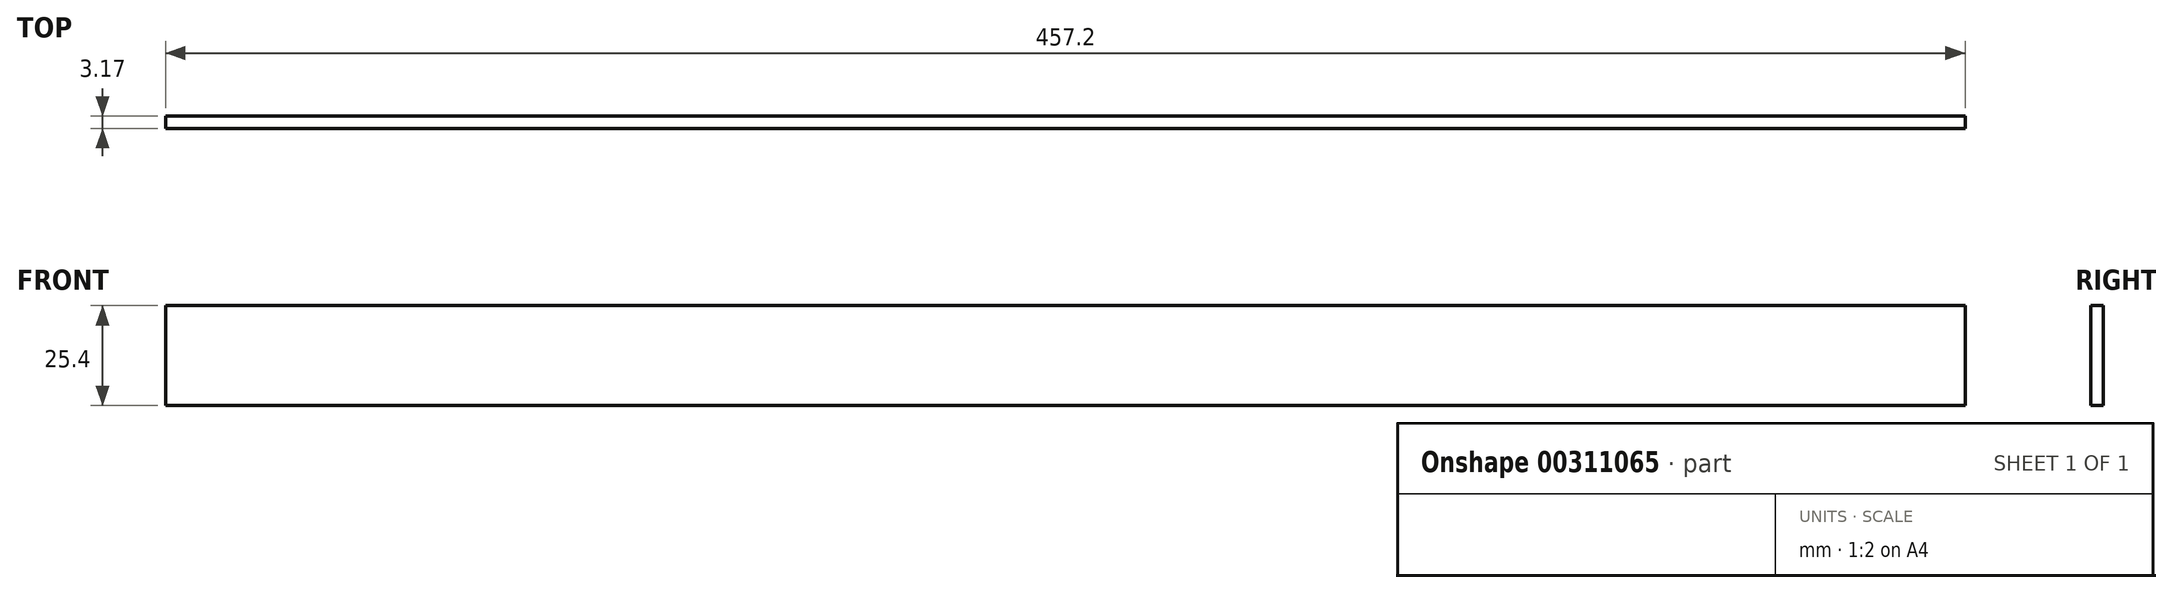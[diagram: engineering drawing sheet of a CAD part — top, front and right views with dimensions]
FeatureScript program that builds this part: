
annotation { "Feature Type Name" : "Feature", "Feature Type Description" : "" }
export const myFeature = defineFeature(function(context is Context, id is Id, definition is map)
    precondition{}
    {
        {
            var Q0;
            Q0=qCreatedBy(makeId("Front.planeOp"),FACE);
            var sketch = newSketch(context, id + "F0", { "sketchPlane" : qUnion([Q0])});
            skLineSegment(sketch, "E0.bottom", {"start": v(0, 0) * mm, "end": v(457.2, 0) * mm});
            skLineSegment(sketch, "E0.top", {"start": v(0, 25.4) * mm, "end": v(457.2, 25.4) * mm});
            skLineSegment(sketch, "E0.left", {"start": v(0, 0) * mm, "end": v(0, 25.4) * mm});
            skLineSegment(sketch, "E0.right", {"start": v(457.2, 0) * mm, "end": v(457.2, 25.4) * mm});
            skSolve(sketch);
        }
        {
            var Q0;
            Q0 = qSketchRegion(id + "F0", true);
            extrude(context, id + "F1", {"entities" : qUnion([Q0]), "depth" : 3.17 * mm});
        }
    });
